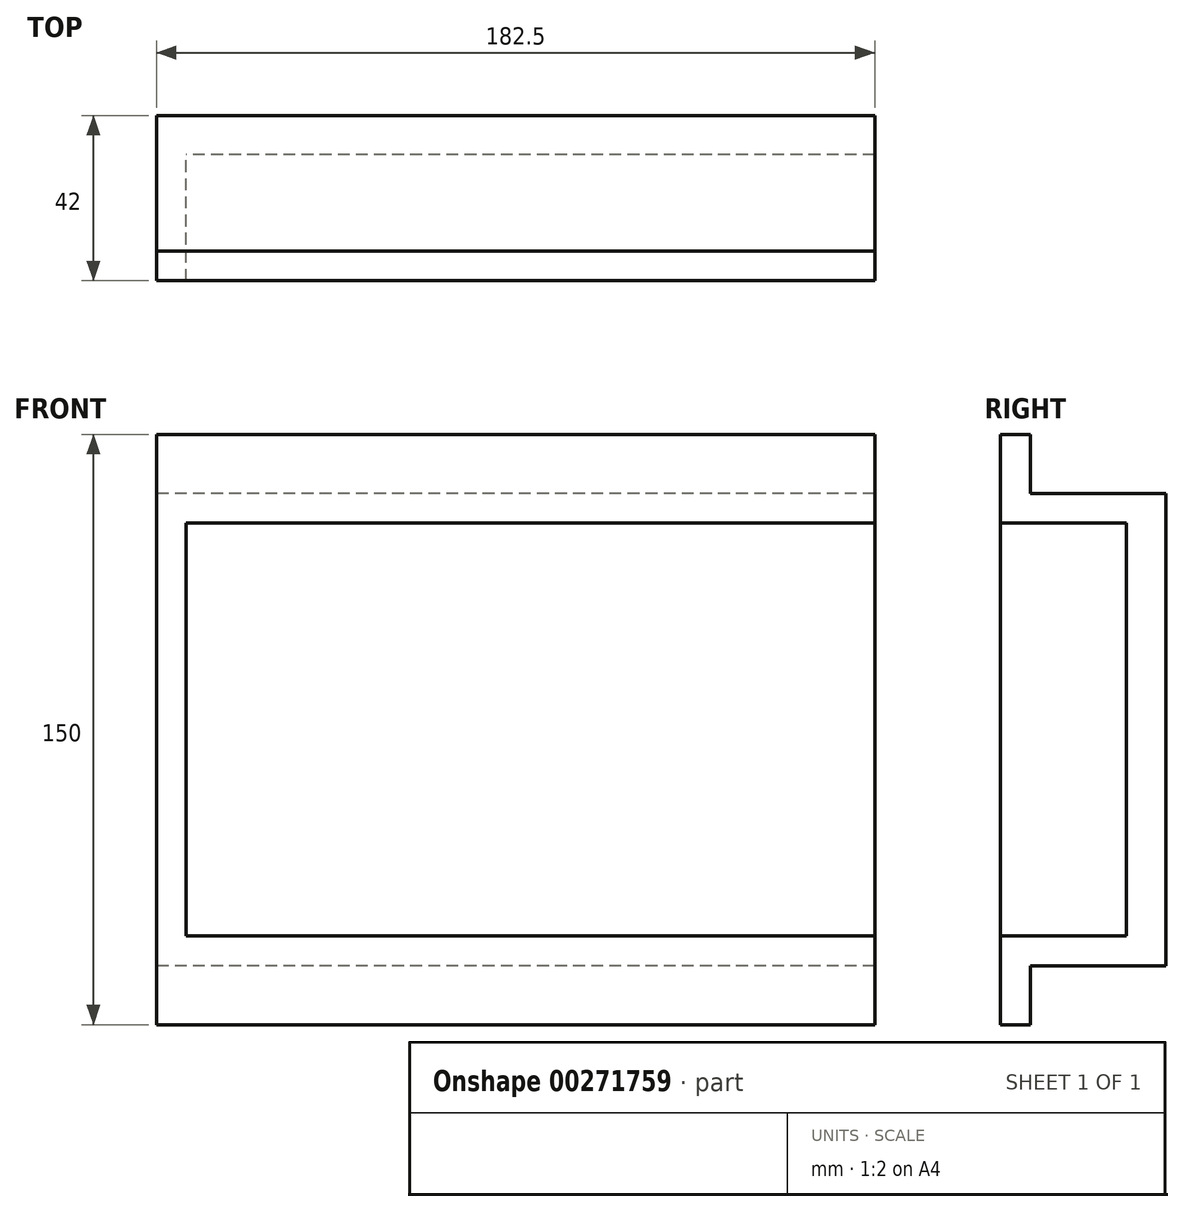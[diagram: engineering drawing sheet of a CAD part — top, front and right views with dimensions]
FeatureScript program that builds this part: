
annotation { "Feature Type Name" : "Feature", "Feature Type Description" : "" }
export const myFeature = defineFeature(function(context is Context, id is Id, definition is map)
    precondition{}
    {
        {
            var Q0;
            Q0=qCreatedBy(makeId("Front.planeOp"),FACE);
            var sketch = newSketch(context, id + "F0", { "sketchPlane" : qUnion([Q0])});
            skLineSegment(sketch, "E0.bottom", {"start": v(87.5, 52.5) * mm, "end": v(-87.5, 52.5) * mm});
            skLineSegment(sketch, "E0.top", {"start": v(87.5, -52.5) * mm, "end": v(-87.5, -52.5) * mm});
            skLineSegment(sketch, "E0.left", {"start": v(87.5, 52.5) * mm, "end": v(87.5, -52.5) * mm});
            skLineSegment(sketch, "E0.right", {"start": v(-87.5, 52.5) * mm, "end": v(-87.5, -52.5) * mm});
            skPoint(sketch, "E0.middle", {"position": v(0, 0) * mm});
            skLineSegment(sketch, "E1.bottom", {"start": v(95, 60) * mm, "end": v(-95, 60) * mm});
            skLineSegment(sketch, "E1.top", {"start": v(95, -60) * mm, "end": v(-95, -60) * mm});
            skLineSegment(sketch, "E1.right", {"start": v(-95, 60) * mm, "end": v(-95, -60) * mm});
            skLineSegment(sketch, "E2", {"start": v(87.5, 52.5) * mm, "end": v(87.5, 60) * mm});
            skLineSegment(sketch, "E3", {"start": v(87.5, -52.5) * mm, "end": v(87.5, -60) * mm});
            skSolve(sketch);
        }
        {
            var Q0;
            Q0=makeQuery(id+"F0.imprint","IMPRINT",FACE,{"disambiguationData":[TD([[makeQuery(id+"F0.imprint","IMPRINT",EDGE,{"derivedFrom":sQuery(id+"F0.wireOp",EDGE,"E0.bottom")}),1.0]])]});
            extrude(context, id + "F1", {"entities" : qUnion([Q0]), "depth" : 10 * mm});
        }
        {
            var Q0;
            Q0=makeQuery(id+"F0.imprint","IMPRINT",FACE,{"disambiguationData":[TD([[makeQuery(id+"F0.imprint","IMPRINT",EDGE,{"derivedFrom":sQuery(id+"F0.wireOp",EDGE,"E0.bottom")}),-1.0]])]});
            extrude(context, id + "F2", {"entities" : qUnion([Q0]), "operationType" : NewBodyOperationType.ADD, "depth" : 42 * mm});
        }
        {
            var Q0;
            Q0=makeQuery(id+"F2.opExtrude","CAP_FACE",FACE,{"disambiguationData":[OSD([sQuery(id+"F0.wireOp",EDGE,"E0.bottom"),sQuery(id+"F0.wireOp",EDGE,"E0.top"),sQuery(id+"F0.wireOp",EDGE,"E0.right"),sQuery(id+"F0.wireOp",EDGE,"E1.bottom"),sQuery(id+"F0.wireOp",EDGE,"E1.top"),sQuery(id+"F0.wireOp",EDGE,"E1.right"),sQuery(id+"F0.wireOp",EDGE,"E2"),sQuery(id+"F0.wireOp",EDGE,"E3")])],"isStart":false});
            var sketch = newSketch(context, id + "F3", { "sketchPlane" : qUnion([Q0])});
            skLineSegment(sketch, "E4.bottom", {"start": v(-95, 60) * mm, "end": v(87.5, 60) * mm});
            skLineSegment(sketch, "E4.top", {"start": v(-95, 75) * mm, "end": v(87.5, 75) * mm});
            skLineSegment(sketch, "E4.left", {"start": v(-95, 60) * mm, "end": v(-95, 75) * mm});
            skLineSegment(sketch, "E4.right", {"start": v(87.5, 60) * mm, "end": v(87.5, 75) * mm});
            skLineSegment(sketch, "E5.bottom", {"start": v(-95, -60) * mm, "end": v(87.5, -60) * mm});
            skLineSegment(sketch, "E5.top", {"start": v(-95, -75) * mm, "end": v(87.5, -75) * mm});
            skLineSegment(sketch, "E5.left", {"start": v(-95, -60) * mm, "end": v(-95, -75) * mm});
            skLineSegment(sketch, "E5.right", {"start": v(87.5, -60) * mm, "end": v(87.5, -75) * mm});
            skSolve(sketch);
        }
        {
            var Q0;
            Q0=makeQuery(id+"F3.imprint","IMPRINT",FACE,{"disambiguationData":[TD([[makeQuery(id+"F3.imprint","IMPRINT",EDGE,{"derivedFrom":sQuery(id+"F3.wireOp",EDGE,"E4.bottom")}),-1.0]])]});
            var Q1;
            Q1=makeQuery(id+"F3.imprint","IMPRINT",FACE,{"disambiguationData":[TD([[makeQuery(id+"F3.imprint","IMPRINT",EDGE,{"derivedFrom":sQuery(id+"F3.wireOp",EDGE,"E5.bottom")}),1.0]])]});
            extrude(context, id + "F4", {"entities" : qUnion([Q0, Q1]), "operationType" : NewBodyOperationType.ADD, "oppositeDirection" : true, "depth" : 7.5 * mm});
        }
    });
